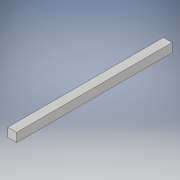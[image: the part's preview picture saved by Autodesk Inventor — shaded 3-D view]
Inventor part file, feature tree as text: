
AUTODESK INVENTOR PART (.ipt)
format: ipt  version: 2019 (Build 230136000, 136)  size: 92,160 bytes
history: native  units: mm
features: extrude x1, sketch x1
ambient origin geometry x8: Origin, YZ Plane, XZ Plane, XY Plane, X Axis, Y Axis, Z Axis, Center Point
bodies: Solid1 (feature_tree)
feature tree (2):
  extrude  "Extrusion1"  Depth=335.0mm
  sketch  "Sketch1"  dims[d0=19.0mm d1=335.0mm d2=19.0mm d3=0.0mm]
